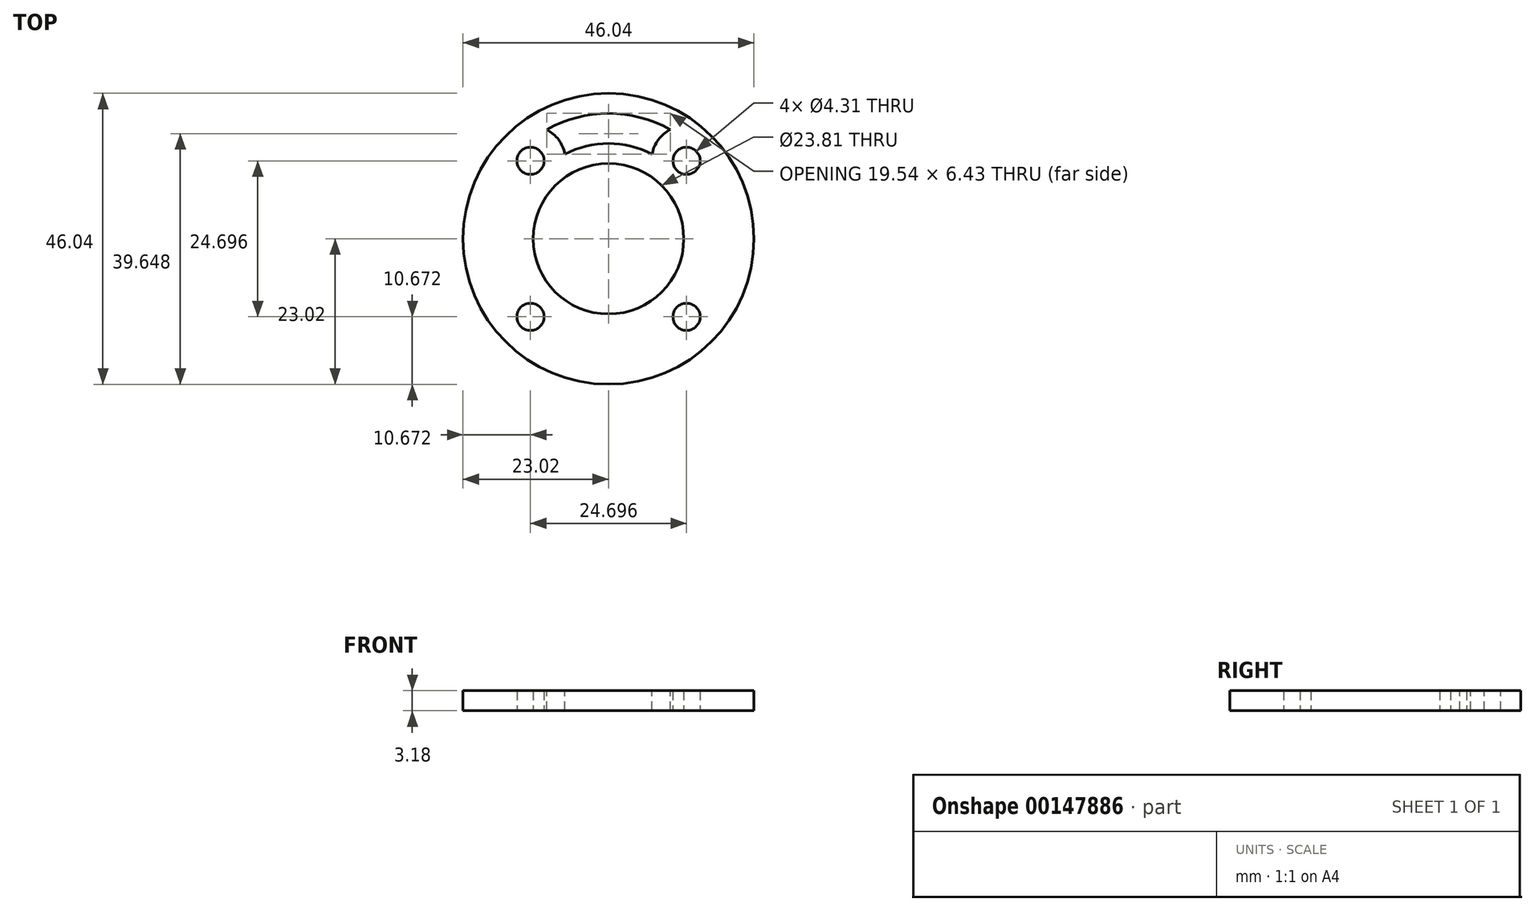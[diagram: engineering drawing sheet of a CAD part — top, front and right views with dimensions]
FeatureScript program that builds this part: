
annotation { "Feature Type Name" : "Feature", "Feature Type Description" : "" }
export const myFeature = defineFeature(function(context is Context, id is Id, definition is map)
    precondition{}
    {
        {
            var Q0;
            Q0=qCreatedBy(makeId("Top.planeOp"),FACE);
            var sketch = newSketch(context, id + "F0", { "sketchPlane" : qUnion([Q0])});
            skCircle(sketch, "E0", {"center": v(0, 0) * mm, "radius": 23.02 * mm});
            skCircle(sketch, "E1", {"center": v(0, 0) * mm, "radius": 11.9 * mm});
            skLineSegment(sketch, "E2.bottom", {"start": v(-12.35, 12.35) * mm, "end": v(12.35, 12.35) * mm, "construction": true});
            skLineSegment(sketch, "E2.top", {"start": v(-12.35, -12.35) * mm, "end": v(12.35, -12.35) * mm, "construction": true});
            skLineSegment(sketch, "E2.left", {"start": v(-12.35, 12.35) * mm, "end": v(-12.35, -12.35) * mm, "construction": true});
            skLineSegment(sketch, "E2.right", {"start": v(12.35, 12.35) * mm, "end": v(12.35, -12.35) * mm, "construction": true});
            skCircle(sketch, "E3", {"center": v(-12.35, 12.35) * mm, "radius": 5.56 * mm, "construction": true});
            skCircle(sketch, "E4", {"center": v(12.35, 12.35) * mm, "radius": 2.15 * mm});
            skCircle(sketch, "E5", {"center": v(-12.35, 12.35) * mm, "radius": 2.15 * mm});
            skCircle(sketch, "E6", {"center": v(-12.35, -12.35) * mm, "radius": 2.15 * mm});
            skCircle(sketch, "E7", {"center": v(12.35, -12.35) * mm, "radius": 2.15 * mm});
            skSolve(sketch);
        }
        {
            var Q0;
            Q0=qSketchRegion(id+"F0",true);
            extrude(context, id + "F1", {"entities" : qUnion([Q0]), "depth" : 3.17 * mm});
        }
        {
            var Q0;
            Q0=makeQuery(id+"F1.opExtrude","CAP_FACE",FACE,{"disambiguationData":[OSD([sQuery(id+"F0.wireOp",EDGE,"E0"),sQuery(id+"F0.wireOp",EDGE,"E1"),sQuery(id+"F0.wireOp",EDGE,"E4"),sQuery(id+"F0.wireOp",EDGE,"E5"),sQuery(id+"F0.wireOp",EDGE,"E6"),sQuery(id+"F0.wireOp",EDGE,"E7")])],"isStart":false});
            var sketch = newSketch(context, id + "F2", { "sketchPlane" : qUnion([Q0])});
            skArc(sketch, "E8", {"start": v(-6.9, 13.41) * mm, "mid": v(-7.9, 15.67) * mm, "end": v(-9.77, 17.27) * mm});
            skArc(sketch, "E9", {"start": v(9.77, 17.27) * mm, "mid": v(7.9, 15.67) * mm, "end": v(6.9, 13.41) * mm});
            skArc(sketch, "E10", {"start": v(9.77, 17.27) * mm, "mid": v(0, 19.84) * mm, "end": v(-9.77, 17.27) * mm});
            skArc(sketch, "E11", {"start": v(6.9, 13.41) * mm, "mid": v(0, 15.08) * mm, "end": v(-6.9, 13.41) * mm});
            skSolve(sketch);
        }
        {
            var Q0;
            Q0=makeQuery(id+"F2.imprint","IMPRINT",FACE,{"disambiguationData":[TD([[makeQuery(id+"F2.imprint","IMPRINT",EDGE,{"derivedFrom":sQuery(id+"F2.wireOp",EDGE,"E8")}),-1.0]])]});
            var Q1;
            Q1=makeQuery(id+"F1.opExtrude","CAP_FACE",FACE,{"disambiguationData":[OSD([sQuery(id+"F0.wireOp",EDGE,"E0"),sQuery(id+"F0.wireOp",EDGE,"E1"),sQuery(id+"F0.wireOp",EDGE,"E4"),sQuery(id+"F0.wireOp",EDGE,"E5"),sQuery(id+"F0.wireOp",EDGE,"E6"),sQuery(id+"F0.wireOp",EDGE,"E7")])],"isStart":true});
            extrude(context, id + "F3", {"entities" : qUnion([Q0]), "operationType" : NewBodyOperationType.REMOVE, "endBound" : BoundingType.UP_TO_SURFACE, "oppositeDirection" : true, "endBoundEntityFace" : qUnion([Q1]), "depth" : 25.4 * mm});
        }
    });
